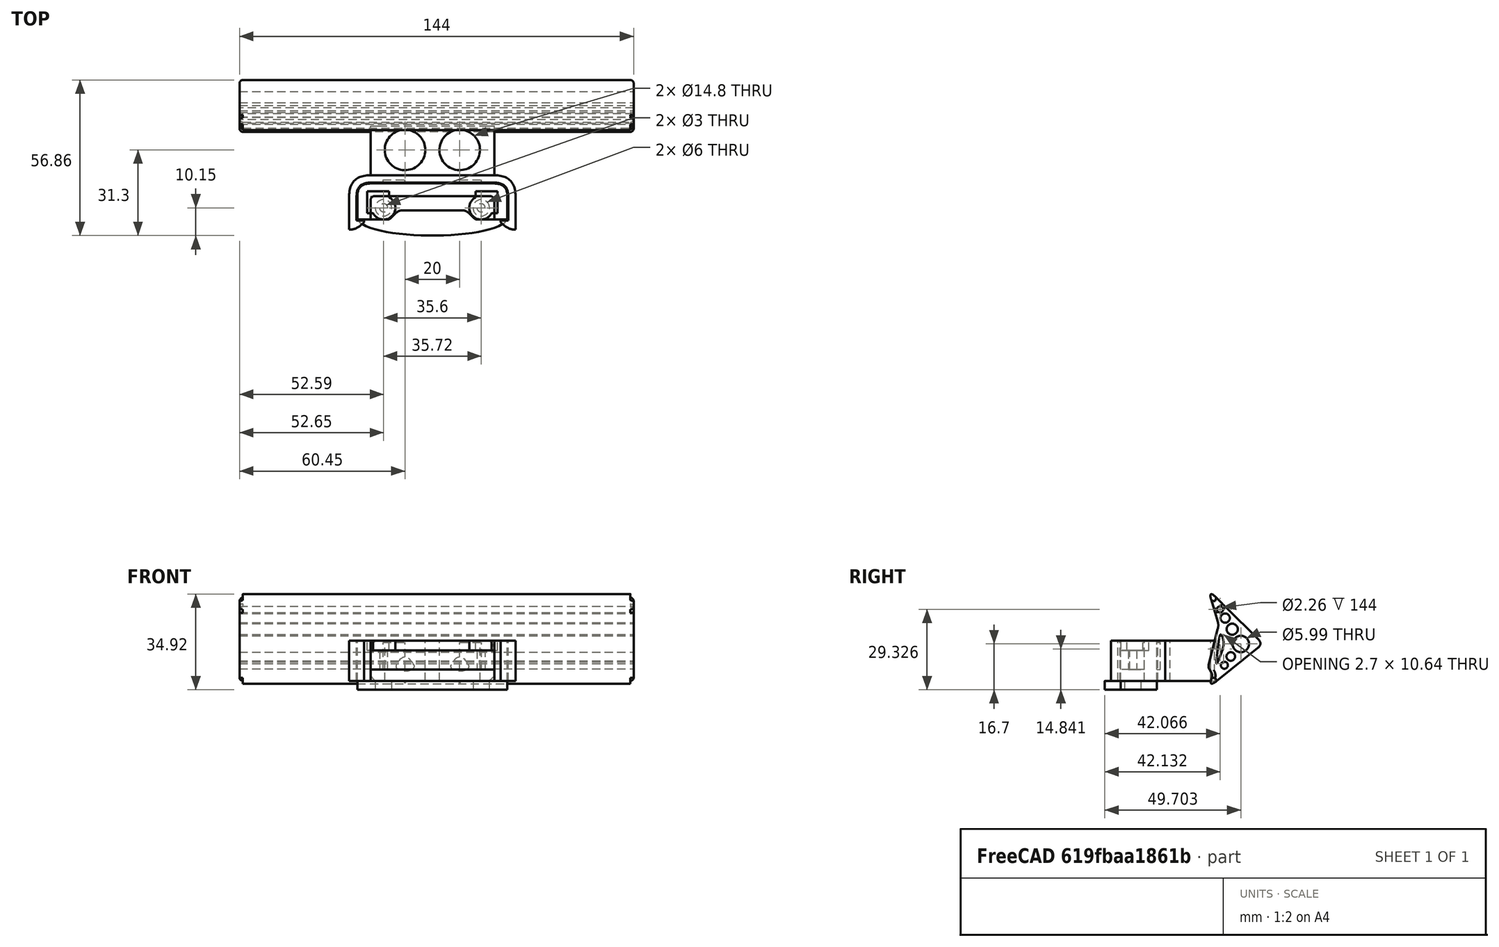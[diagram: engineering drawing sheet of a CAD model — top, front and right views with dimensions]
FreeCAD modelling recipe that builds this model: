
FCSTD DOCUMENT  (FreeCAD 0.19R0.19.2)
Label: 037
License: All rights reserved
LicenseURL: http://en.wikipedia.org/wiki/All_rights_reserved
objects: Sketcher::SketchObject×6, Part::Extrusion×6, Part::Cylinder×4, Part::Box×3, Part::Fillet×3, Part::MultiFuse×2, Part::Cut×2
note: 26 computed .brp shape members not serialized (recipe doc carries the construction recipe); baked Part::Feature solids carry a one-line shape summary decoded from their .brp

FEATURE [Sketcher::SketchObject] Sketch  label="attatchmentPiece"
  FullyConstrained = true
  sketch-geometry (20):
    g0: Circle CenterX=16.25 CenterY=0 CenterZ=0 NormalX=0 NormalY=0 NormalZ=1 AngleXU=0 Radius=1.5
    g1: LineSegment StartX=21.05 StartY=0 StartZ=0 EndX=21.05 EndY=-1 EndZ=0
    g2: LineSegment StartX=21.05 StartY=-1 StartZ=0 EndX=21.05 EndY=-4.3 EndZ=0
    g3: LineSegment StartX=-24.15 StartY=4.3 StartZ=0 EndX=21.05 EndY=4.3 EndZ=0
    g4: LineSegment StartX=21.05 StartY=0 StartZ=0 EndX=21.05 EndY=4.3 EndZ=0
    g5-g8: Circle x4 (B-spline internal-alignment scaffolding for g9; pole/knot coordinates omitted)
    g9: BSplineCurve PolesCount=4 KnotsCount=2 Degree=3 IsPeriodic=0
    g10: GeomPoint X=10.05 Y=-1 Z=0
    g11: GeomPoint X=14.55 Y=-4.3 Z=0
    g12: LineSegment StartX=10.05 StartY=-1 StartZ=0 EndX=-10.05 EndY=-1 EndZ=0
    g13: LineSegment StartX=14.55 StartY=-4.3 StartZ=0 EndX=21.05 EndY=-4.3 EndZ=0
    g14: LineSegment StartX=-24.15 StartY=4.3 StartZ=0 EndX=-24.15 EndY=-4.3 EndZ=0
    g15: LineSegment StartX=-13.15 StartY=-1 StartZ=0 EndX=-10.05 EndY=-1 EndZ=0
    g16: LineSegment StartX=-24.15 StartY=-4.3 StartZ=0 EndX=-19.35 EndY=-4.3 EndZ=0
    g17: Circle CenterX=-19.35 CenterY=0 CenterZ=0 NormalX=0 NormalY=0 NormalZ=1 AngleXU=0 Radius=1.5
    g18: LineSegment StartX=-19.35 StartY=-4.3 StartZ=0 EndX=-17.65 EndY=-4.3 EndZ=0
    g19: BSplineCurve PolesCount=4 KnotsCount=2 Degree=3 IsPeriodic=0
  constraints (41):
    c: Block(g0)
    c: Vertical(g1)
    c: Coincident(g2,g1)
    c: Vertical(g2)
    c: Block(g1)
    c: Horizontal(g3)
    c: Vertical(g4)
    c: Coincident(g4,g3)
    c: Block(g3)
    c: Block(g4)
    c: Weight(g5) = 1
    c: Equal(g5,g6)
    c: Equal(g5,g7)
    c: Equal(g5,g8)
    c: InternalAlignment(g5-g8 -> g9) x4
    c: InternalAlignment(g10,g9)
    c: InternalAlignment(g11,g9)
    c: Block(g9)
    c: Coincident(g12,g9)
    c: Horizontal(g12)
    c: Coincident(g13,g9)
    c: Coincident(g13,g2)
    c: Horizontal(g13)
    c: Distance(g3) = 45.2
    c: Coincident(g14,g3)
    c: Vertical(g14)
    c: Horizontal(g15)
    c: Distance(g15) = 3.1
    c: Block(g17)
    c: Horizontal(g16)
    c: Block(g19)
    c: Coincident(g18,g16)
    c: Coincident(g18,g19)
    c: Horizontal(g18)
    c: Block(g18)
    c: Coincident(g19,g15)
    c: Block(g16)
    c: Block(g12)
    c: Block(g14)
    c: Distance(g16) = 4.8
    c: Distance(g18) = 1.7
FEATURE [Part::Extrusion] Extrude  label="attatchmentPiece001"
  Base = -> Sketch
  Dir = (0,0,1)
  DirMode = 2
  FaceMakerClass = Part::FaceMakerBullseye
  LengthFwd = 7
  LengthRev = 0
  Solid = true
  Symmetric = false
FEATURE [Sketcher::SketchObject] Sketch001  label="attatchmentPieceSurround"
  FullyConstrained = true
  sketch-geometry (18):
    g0: LineSegment StartX=25.85 StartY=-4.3 StartZ=0 EndX=21.05 EndY=-4.3 EndZ=0
    g1: LineSegment StartX=25.85 StartY=-4.3 StartZ=0 EndX=25.85 EndY=4.3 EndZ=0
    g2: LineSegment StartX=-21.05 StartY=8.9 StartZ=0 EndX=21.05 EndY=8.9 EndZ=0
    g3: Circle CenterX=21.05 CenterY=8.9 CenterZ=0 NormalX=0 NormalY=0 NormalZ=1 AngleXU=0 Radius=1
    g4: Circle CenterX=25.85 CenterY=8.9 CenterZ=0 NormalX=0 NormalY=0 NormalZ=1 AngleXU=0 Radius=1
    g5: Circle CenterX=25.85 CenterY=4.3 CenterZ=0 NormalX=0 NormalY=0 NormalZ=1 AngleXU=0 Radius=1
    g6: BSplineCurve PolesCount=3 KnotsCount=2 Degree=2 IsPeriodic=0
    g7: GeomPoint X=21.05 Y=8.9 Z=0
    g8: GeomPoint X=25.85 Y=4.3 Z=0
    g9: ArcOfCircle CenterX=19.45 CenterY=2.7 CenterZ=0 NormalX=0 NormalY=0 NormalZ=1 AngleXU=0 Radius=1.6 StartAngle=0 EndAngle=1.5708
    g10: LineSegment StartX=21.05 StartY=2.7 StartZ=0 EndX=21.05 EndY=-4.3 EndZ=0
    g11: BSplineCurve PolesCount=3 KnotsCount=2 Degree=2 IsPeriodic=0
    g12: LineSegment StartX=-28.95 StartY=-4.3 StartZ=0 EndX=-28.95 EndY=4.3 EndZ=0
    g13: LineSegment StartX=-24.15 StartY=-4.3 StartZ=0 EndX=-28.95 EndY=-4.3 EndZ=0
    g14: LineSegment StartX=-24.15 StartY=2.7 StartZ=0 EndX=-24.15 EndY=-4.3 EndZ=0
    g15: ArcOfCircle CenterX=-22.55 CenterY=2.7 CenterZ=0 NormalX=0 NormalY=0 NormalZ=1 AngleXU=0 Radius=1.6 StartAngle=1.5708 EndAngle=3.14159
    g16: LineSegment StartX=-24.15 StartY=8.9 StartZ=0 EndX=-21.05 EndY=8.9 EndZ=0
    g17: LineSegment StartX=-22.55 StartY=4.3 StartZ=0 EndX=19.45 EndY=4.3 EndZ=0
  constraints (38):
    c: Horizontal(g0)
    c: Vertical(g1)
    c: Coincident(g1,g0)
    c: Horizontal(g2)
    c: Distance(g2) = 42.1
    c: Block(g2)
    c: Coincident(g6,g2)
    c: Weight(g3) = 1
    c: Equal(g3,g4)
    c: Equal(g3,g5)
    c: Coincident(g6,g1)
    c: InternalAlignment(g3,g6)
    c: InternalAlignment(g4,g6)
    c: InternalAlignment(g5,g6)
    c: InternalAlignment(g7,g6)
    c: InternalAlignment(g8,g6)
    c: Block(g0)
    c: Block(g6)
    c: Block(g9)
    c: Coincident(g10,g9)
    c: Coincident(g10,g0)
    c: Vertical(g10)
    c: Horizontal(g13)
    c: Coincident(g12,g13)
    c: Vertical(g12)
    c: Coincident(g11,g12)
    c: Block(g12)
    c: Block(g11)
    c: Block(g15)
    c: Coincident(g14,g15)
    c: Coincident(g14,g13)
    c: Vertical(g14)
    c: Coincident(g16,g11)
    c: Coincident(g16,g2)
    c: Horizontal(g16)
    c: Coincident(g17,g15)
    c: Coincident(g17,g9)
    c: Horizontal(g17)
FEATURE [Part::Extrusion] Extrude001  label="attatchmentPieceSurround001"
  Base = -> Sketch001
  Dir = (0,0,1)
  DirMode = 2
  FaceMakerClass = Part::FaceMakerBullseye
  LengthFwd = 14.7
  LengthRev = 0
  Placement = pos=(0,0,-4.1) rot=(0,0,1;0rad)
  Solid = true
  Symmetric = false
FEATURE [Sketcher::SketchObject] Sketch002  label="attatchmentPieceEndScrewHoleCaps"
  FullyConstrained = true
  sketch-geometry (10):
    g0: ArcOfCircle CenterX=16.25 CenterY=0 CenterZ=0 NormalX=0 NormalY=0 NormalZ=1 AngleXU=0 Radius=4.3 StartAngle=2.05456 EndAngle=5.79942
    g1: LineSegment StartX=14.25 StartY=3.80657 StartZ=0 EndX=14.25 EndY=6 EndZ=0
    g2: LineSegment StartX=20.0566 StartY=-2 StartZ=0 EndX=22.25 EndY=-2 EndZ=0
    g3: LineSegment StartX=22.25 StartY=-2 StartZ=0 EndX=22.25 EndY=6 EndZ=0
    g4: LineSegment StartX=14.25 StartY=6 StartZ=0 EndX=22.25 EndY=6 EndZ=0
    g5: LineSegment StartX=-25.35 StartY=-2 StartZ=0 EndX=-25.35 EndY=6 EndZ=0
    g6: LineSegment StartX=-25.35 StartY=-2 StartZ=0 EndX=-23.1566 EndY=-2 EndZ=0
    g7: LineSegment StartX=-17.35 StartY=6 StartZ=0 EndX=-25.35 EndY=6 EndZ=0
    g8: LineSegment StartX=-17.35 StartY=3.80657 StartZ=0 EndX=-17.35 EndY=6 EndZ=0
    g9: ArcOfCircle CenterX=-19.35 CenterY=0 CenterZ=0 NormalX=0 NormalY=0 NormalZ=1 AngleXU=0 Radius=4.3 StartAngle=3.62536 EndAngle=7.37022
  constraints (25):
    c: Block(g0)
    c: Vertical(g1)
    c: Horizontal(g2)
    c: Coincident(g3,g2)
    c: Vertical(g3)
    c: Coincident(g4,g1)
    c: Horizontal(g4)
    c: Coincident(g3,g4)
    c: Block(g4)
    c: Block(g3)
    c: Coincident(g0,g1)
    c: Coincident(g0,g2)
    c: Block(g1)
    c: Block(g9)
    c: Horizontal(g6)
    c: Vertical(g8)
    c: Coincident(g7,g8)
    c: Horizontal(g7)
    c: Coincident(g5,g6)
    c: Vertical(g5)
    c: Coincident(g5,g7)
    c: Block(g7)
    c: Block(g5)
    c: Coincident(g9,g6)
    c: Coincident(g9,g8)
FEATURE [Part::Extrusion] Extrude002  label="attatchmentPieceEndScrewHoleCaps001"
  Base = -> Sketch002
  Dir = (0,0,1)
  DirMode = 2
  FaceMakerClass = Part::FaceMakerBullseye
  LengthFwd = 3.6
  LengthRev = 0
  Placement = pos=(0,0,7) rot=(0,0,1;0rad)
  Solid = true
  Symmetric = false
FEATURE [Sketcher::SketchObject] Sketch003  label="mainBumpperPieceAttatchment"
  FullyConstrained = true
  sketch-geometry (42):
    g0: Circle CenterX=28.85 CenterY=4.3 CenterZ=0 NormalX=0 NormalY=0 NormalZ=1 AngleXU=0 Radius=1
    g1: Circle CenterX=28.85 CenterY=11.9 CenterZ=0 NormalX=0 NormalY=0 NormalZ=1 AngleXU=0 Radius=1
    g2: Circle CenterX=21.05 CenterY=11.9 CenterZ=0 NormalX=0 NormalY=0 NormalZ=1 AngleXU=0 Radius=1
    g3: BSplineCurve PolesCount=3 KnotsCount=2 Degree=2 IsPeriodic=0
    g4: GeomPoint X=28.85 Y=4.3 Z=0
    g5: GeomPoint X=21.05 Y=11.9 Z=0
    g6: LineSegment StartX=-21.05 StartY=11.9 StartZ=0 EndX=21.05 EndY=11.9 EndZ=0
    g7: LineSegment StartX=28.85 StartY=4.3 StartZ=0 EndX=28.85 EndY=-4.3 EndZ=0
    g8: Circle CenterX=21.05 CenterY=9.2 CenterZ=0 NormalX=0 NormalY=0 NormalZ=1 AngleXU=0 Radius=1
    g9: Circle CenterX=26.15 CenterY=9.2 CenterZ=0 NormalX=0 NormalY=0 NormalZ=1 AngleXU=0 Radius=1
    g10: Circle CenterX=26.15 CenterY=4.3 CenterZ=0 NormalX=0 NormalY=0 NormalZ=1 AngleXU=0 Radius=1
    g11: BSplineCurve PolesCount=3 KnotsCount=2 Degree=2 IsPeriodic=0
    g12: GeomPoint X=21.05 Y=9.2 Z=0
    g13: GeomPoint X=26.15 Y=4.3 Z=0
    g14: LineSegment StartX=-21.05 StartY=9.2 StartZ=0 EndX=21.05 EndY=9.2 EndZ=0
    g15: LineSegment StartX=26.15 StartY=-4.3 StartZ=0 EndX=26.15 EndY=4.3 EndZ=0
    g16: LineSegment StartX=26.15 StartY=-4.3 StartZ=0 EndX=26.15 EndY=-4.6 EndZ=0
    g17: LineSegment StartX=23.45 StartY=-4.6 StartZ=0 EndX=26.15 EndY=-4.6 EndZ=0
    g18: LineSegment StartX=28.85 StartY=-4.3 StartZ=0 EndX=28.85 EndY=-7.9 EndZ=0
    g19: LineSegment StartX=23.45 StartY=-4.6 StartZ=0 EndX=23.45 EndY=-5.3 EndZ=0
    g20: Circle CenterX=28.85 CenterY=-7.9 CenterZ=0 NormalX=0 NormalY=0 NormalZ=1 AngleXU=0 Radius=1
    g21: Circle CenterX=26.15 CenterY=-8.2 CenterZ=0 NormalX=0 NormalY=0 NormalZ=1 AngleXU=0 Radius=1
    g22: Circle CenterX=23.45 CenterY=-5.3 CenterZ=0 NormalX=0 NormalY=0 NormalZ=1 AngleXU=0 Radius=1
    g23: BSplineCurve PolesCount=3 KnotsCount=2 Degree=2 IsPeriodic=0
    g24: GeomPoint X=28.85 Y=-7.9 Z=0
    g25: GeomPoint X=23.45 Y=-5.3 Z=0
    g26: LineSegment StartX=-21.05 StartY=9.2 StartZ=0 EndX=-24.15 EndY=9.2 EndZ=0
    g27: BSplineCurve PolesCount=3 KnotsCount=2 Degree=2 IsPeriodic=0
    g28: LineSegment StartX=-29.25 StartY=-4.3 StartZ=0 EndX=-29.25 EndY=-4.6 EndZ=0
    g29: LineSegment StartX=-29.25 StartY=-4.6 StartZ=0 EndX=-26.55 EndY=-4.6 EndZ=0
    g30: LineSegment StartX=-31.95 StartY=-4.3 StartZ=0 EndX=-31.95 EndY=-7.9 EndZ=0
    g31: LineSegment StartX=-26.55 StartY=-4.6 StartZ=0 EndX=-26.55 EndY=-5.3 EndZ=0
    g32: Circle CenterX=-31.95 CenterY=-7.9 CenterZ=0 NormalX=0 NormalY=0 NormalZ=1 AngleXU=0 Radius=1
    g33: Circle CenterX=-29.25 CenterY=-8.2 CenterZ=0 NormalX=0 NormalY=0 NormalZ=1 AngleXU=0 Radius=1
    g34: Circle CenterX=-26.55 CenterY=-5.3 CenterZ=0 NormalX=0 NormalY=0 NormalZ=1 AngleXU=0 Radius=1
    g35: BSplineCurve PolesCount=3 KnotsCount=2 Degree=2 IsPeriodic=0
    g36: GeomPoint X=-31.95 Y=-7.9 Z=0
    g37: GeomPoint X=-26.55 Y=-5.3 Z=0
    g38: LineSegment StartX=-31.95 StartY=4.3 StartZ=0 EndX=-31.95 EndY=-4.3 EndZ=0
    g39: LineSegment StartX=-29.25 StartY=-4.3 StartZ=0 EndX=-29.25 EndY=4.3 EndZ=0
    g40: BSplineCurve PolesCount=3 KnotsCount=2 Degree=2 IsPeriodic=0
    g41: LineSegment StartX=-21.05 StartY=11.9 StartZ=0 EndX=-24.15 EndY=11.9 EndZ=0
  constraints (78):
    c: Weight(g0) = 1
    c: Equal(g0,g1)
    c: Equal(g0,g2)
    c: InternalAlignment(g0,g3)
    c: InternalAlignment(g1,g3)
    c: InternalAlignment(g2,g3)
    c: InternalAlignment(g4,g3)
    c: InternalAlignment(g5,g3)
    c: Block(g3)
    c: Horizontal(g6)
    c: Vertical(g7)
    c: Block(g7)
    c: Block(g6)
    c: Weight(g8) = 1
    c: Equal(g8,g9)
    c: Equal(g8,g10)
    c: InternalAlignment(g8,g11)
    c: InternalAlignment(g9,g11)
    c: InternalAlignment(g10,g11)
    c: InternalAlignment(g12,g11)
    c: InternalAlignment(g13,g11)
    c: Horizontal(g14)
    c: Vertical(g15)
    c: Block(g11)
    c: Block(g15)
    c: Block(g14)
    c: Coincident(g16,g15)
    c: Vertical(g16)
    c: Distance(g16) = 0.3
    c: Horizontal(g17)
    c: Coincident(g17,g16)
    c: Coincident(g18,g7)
    c: Vertical(g18)
    c: Distance(g18) = 3.6
    c: Vertical(g19)
    c: Coincident(g19,g17)
    c: Coincident(g23,g18)
    c: Weight(g20) = 1
    c: Equal(g20,g21)
    c: Equal(g20,g22)
    c: Coincident(g23,g19)
    c: InternalAlignment(g20,g23)
    c: InternalAlignment(g21,g23)
    c: InternalAlignment(g22,g23)
    c: InternalAlignment(g24,g23)
    c: InternalAlignment(g25,g23)
    c: Block(g23)
    c: Horizontal(g26)
    c: Distance(g26) = 3.1
    c: Block(g27)
    c: Vertical(g38)
    c: Block(g38)
    c: Vertical(g39)
    c: Block(g40)
    c: Block(g39)
    c: Vertical(g28)
    c: Coincident(g28,g39)
    c: Coincident(g29,g28)
    c: Horizontal(g29)
    c: Vertical(g30)
    c: Coincident(g30,g38)
    c: Coincident(g31,g29)
    c: Vertical(g31)
    c: Coincident(g35,g30)
    c: Equal(g32,g33)
    c: Equal(g32,g34)
    c: Coincident(g35,g31)
    c: InternalAlignment(g32,g35)
    c: InternalAlignment(g33,g35)
    c: InternalAlignment(g34,g35)
    c: InternalAlignment(g36,g35)
    c: InternalAlignment(g37,g35)
    c: Block(g35)
    c: Coincident(g40,g26)
    c: Block(g29)
    c: Horizontal(g41)
    c: Equal(g26,g41) = 3.1
    c: Coincident(g41,g6)
FEATURE [Part::Box] Box  label="bumpperExtension"
  AttacherType = Attacher::AttachEngine3D
  Height = 14.7
  Length = 45.2
  Placement = pos=(-24.15,11.9,-4.1) rot=(0,0,1;0rad)
  Width = 18
FEATURE [Sketcher::SketchObject] Sketch004  label="bumpperMain"
  FullyConstrained = true
  Placement = pos=(0,0,0) rot=(0.57735,0.57735,0.57735;2.0944rad)
  sketch-geometry (62):
    g0: Circle CenterX=-3.12329 CenterY=2.49901 CenterZ=0 NormalX=0 NormalY=0 NormalZ=1 AngleXU=0 Radius=1
    g1: Circle CenterX=0 CenterY=0 CenterZ=0 NormalX=0 NormalY=0 NormalZ=1 AngleXU=0 Radius=1
    g2: Circle CenterX=-1.35243 CenterY=3.60648 CenterZ=0 NormalX=0 NormalY=0 NormalZ=1 AngleXU=0 Radius=1
    g3: BSplineCurve PolesCount=3 KnotsCount=2 Degree=2 IsPeriodic=0
    g4: GeomPoint X=-3.12329 Y=2.49901 Z=0
    g5: GeomPoint X=-1.35243 Y=3.60648 Z=0
    g6: Circle CenterX=-2.83953 CenterY=33.0261 CenterZ=0 NormalX=0 NormalY=0 NormalZ=1 AngleXU=0 Radius=1
    g7: Circle CenterX=0 CenterY=35.8434 CenterZ=0 NormalX=0 NormalY=0 NormalZ=1 AngleXU=0 Radius=1
    g8: Circle CenterX=-1.15771 CenterY=32.0146 CenterZ=0 NormalX=0 NormalY=0 NormalZ=1 AngleXU=0 Radius=1
    g9: BSplineCurve PolesCount=3 KnotsCount=2 Degree=2 IsPeriodic=0
    g10: GeomPoint X=-2.83953 Y=33.0261 Z=0
    g11: GeomPoint X=-1.15771 Y=32.0146 Z=0
    g12: Circle CenterX=-18.2963 CenterY=17.6904 CenterZ=0 NormalX=0 NormalY=0 NormalZ=1 AngleXU=0 Radius=1
    g13: Circle CenterX=-20 CenterY=16 CenterZ=0 NormalX=0 NormalY=0 NormalZ=1 AngleXU=0 Radius=1
    g14: Circle CenterX=-18.1259 CenterY=14.5008 CenterZ=0 NormalX=0 NormalY=0 NormalZ=1 AngleXU=0 Radius=1
    g15: BSplineCurve PolesCount=3 KnotsCount=2 Degree=2 IsPeriodic=0
    g16: GeomPoint X=-18.2963 Y=17.6904 Z=0
    g17: GeomPoint X=-18.1259 Y=14.5008 Z=0
    g18: LineSegment StartX=-18.2963 StartY=17.6904 StartZ=0 EndX=-2.83953 EndY=33.0261 EndZ=0
    g19: LineSegment StartX=-18.1259 StartY=14.5008 StartZ=0 EndX=-3.12329 EndY=2.49901 EndZ=0
    g20: Circle CenterX=-11.9527 CenterY=16 CenterZ=0 NormalX=0 NormalY=0 NormalZ=1 AngleXU=0 Radius=2.99582
    g21: Circle CenterX=-8.803 CenterY=21.3731 CenterZ=0 NormalX=0 NormalY=0 NormalZ=1 AngleXU=0 Radius=2.03939
    g22: Circle CenterX=-6.23123 CenterY=25.4475 CenterZ=0 NormalX=0 NormalY=0 NormalZ=1 AngleXU=0 Radius=1.69309
    g23: Circle CenterX=-4.38186 CenterY=28.6261 CenterZ=0 NormalX=0 NormalY=0 NormalZ=1 AngleXU=0 Radius=1.13029
    g24: Circle CenterX=-8.28033 CenterY=11.4296 CenterZ=0 NormalX=0 NormalY=0 NormalZ=1 AngleXU=0 Radius=1.57213
    g25: Circle CenterX=-5.93972 CenterY=8.22213 CenterZ=0 NormalX=0 NormalY=0 NormalZ=1 AngleXU=0 Radius=1.28743
    g26: Circle CenterX=-3.47023 CenterY=24.3665 CenterZ=0 NormalX=0 NormalY=0 NormalZ=1 AngleXU=0 Radius=1
    g27: Circle CenterX=-3.90437 CenterY=22.9307 CenterZ=0 NormalX=0 NormalY=0 NormalZ=1 AngleXU=0 Radius=1
    g28: Circle CenterX=-3.53772 CenterY=21.4762 CenterZ=0 NormalX=0 NormalY=0 NormalZ=1 AngleXU=0 Radius=1
    g29: BSplineCurve PolesCount=3 KnotsCount=2 Degree=2 IsPeriodic=0
    g30: GeomPoint X=-3.47023 Y=24.3665 Z=0
    g31: GeomPoint X=-3.53772 Y=21.4762 Z=0
    g32: LineSegment StartX=-1.15771 StartY=32.0146 StartZ=0 EndX=-3.47023 EndY=24.3665 EndZ=0
    g33: Circle CenterX=-5.41867 CenterY=17.9226 CenterZ=0 NormalX=0 NormalY=0 NormalZ=1 AngleXU=0 Radius=1
    g34: Circle CenterX=-6 CenterY=16 CenterZ=0 NormalX=0 NormalY=0 NormalZ=1 AngleXU=0 Radius=1
    g35: Circle CenterX=-5.22753 CenterY=13.9401 CenterZ=0 NormalX=0 NormalY=0 NormalZ=1 AngleXU=0 Radius=1
    g36: BSplineCurve PolesCount=3 KnotsCount=2 Degree=2 IsPeriodic=0
    g37: GeomPoint X=-5.41867 Y=17.9226 Z=0
    g38: GeomPoint X=-5.22753 Y=13.9401 Z=0
    g39: Circle CenterX=-3.98946 CenterY=10.6386 CenterZ=0 NormalX=0 NormalY=0 NormalZ=1 AngleXU=0 Radius=1
    g40: Circle CenterX=-2.58497 CenterY=6.89324 CenterZ=0 NormalX=0 NormalY=0 NormalZ=1 AngleXU=0 Radius=1
    g41: Circle CenterX=-3.11001 CenterY=10.8586 CenterZ=0 NormalX=0 NormalY=0 NormalZ=1 AngleXU=0 Radius=1
    g42: BSplineCurve PolesCount=3 KnotsCount=2 Degree=2 IsPeriodic=0
    g43: GeomPoint X=-3.98946 Y=10.6386 Z=0
    g44: GeomPoint X=-3.11001 Y=10.8586 Z=0
    g45: Circle CenterX=-1.35243 CenterY=3.60648 CenterZ=0 NormalX=0 NormalY=0 NormalZ=1 AngleXU=0 Radius=1
    g46: Circle CenterX=-1.76142 CenterY=4.69712 CenterZ=0 NormalX=0 NormalY=0 NormalZ=1 AngleXU=0 Radius=1
    g47: Circle CenterX=-1.05937 CenterY=5.79125 CenterZ=0 NormalX=0 NormalY=0 NormalZ=1 AngleXU=0 Radius=1
    g48: BSplineCurve PolesCount=3 KnotsCount=2 Degree=2 IsPeriodic=0
    g49: GeomPoint X=-1.35243 Y=3.60648 Z=0
    g50: GeomPoint X=-1.05937 Y=5.79125 Z=0
    g51: Circle CenterX=-0.519336 CenterY=6.6329 CenterZ=0 NormalX=0 NormalY=0 NormalZ=1 AngleXU=0 Radius=1
    g52: Circle CenterX=0 CenterY=7.44228 CenterZ=0 NormalX=0 NormalY=0 NormalZ=1 AngleXU=0 Radius=1
    g53: Circle CenterX=-0.244436 CenterY=8.41194 CenterZ=0 NormalX=0 NormalY=0 NormalZ=1 AngleXU=0 Radius=1
    g54: BSplineCurve PolesCount=3 KnotsCount=2 Degree=2 IsPeriodic=0
    g55: GeomPoint X=-0.519336 Y=6.6329 Z=0
    g56: GeomPoint X=-0.244436 Y=8.41194 Z=0
    g57: LineSegment StartX=-3.53772 StartY=21.4762 StartZ=0 EndX=-0.244436 EndY=8.41194 EndZ=0
    g58: LineSegment StartX=-5.22753 StartY=13.9401 StartZ=0 EndX=-3.98946 EndY=10.6386 EndZ=0
    g59: LineSegment StartX=-1.05937 StartY=5.79125 StartZ=0 EndX=-0.519336 EndY=6.6329 EndZ=0
    g60: BSplineCurve PolesCount=3 KnotsCount=2 Degree=2 IsPeriodic=0
    g61: LineSegment StartX=-4.0304 StartY=17.8099 StartZ=0 EndX=-3.11001 EndY=10.8586 EndZ=0
  constraints (96):
    c: Weight(g0) = 1
    c: Equal(g0,g1)
    c: Equal(g0,g2)
    c: InternalAlignment(g0,g3)
    c: InternalAlignment(g1,g3)
    c: InternalAlignment(g2,g3)
    c: InternalAlignment(g4,g3)
    c: InternalAlignment(g5,g3)
    c: Block(g3)
    c: Weight(g6) = 1
    c: Equal(g6,g7)
    c: Equal(g6,g8)
    c: InternalAlignment(g6,g9)
    c: InternalAlignment(g7,g9)
    c: InternalAlignment(g8,g9)
    c: InternalAlignment(g10,g9)
    c: InternalAlignment(g11,g9)
    c: Block(g9)
    c: Weight(g12) = 1
    c: Equal(g12,g13)
    c: Equal(g12,g14)
    c: InternalAlignment(g12,g15)
    c: InternalAlignment(g13,g15)
    c: InternalAlignment(g14,g15)
    c: InternalAlignment(g16,g15)
    c: InternalAlignment(g17,g15)
    c: Block(g15)
    c: Coincident(g18,g15)
    c: Coincident(g18,g9)
    c: Coincident(g19,g15)
    c: Coincident(g19,g3)
    c: Block(g25)
    c: Block(g24)
    c: Block(g20)
    c: Block(g21)
    c: Block(g22)
    c: Block(g23)
    c: Weight(g26) = 1
    c: Equal(g26,g27)
    c: Equal(g26,g28)
    c: InternalAlignment(g26,g29)
    c: InternalAlignment(g27,g29)
    c: InternalAlignment(g28,g29)
    c: InternalAlignment(g30,g29)
    c: InternalAlignment(g31,g29)
    c: Block(g29)
    c: Coincident(g32,g9)
    c: Coincident(g32,g29)
    c: Weight(g33) = 1
    c: Equal(g33,g34)
    c: Equal(g33,g35)
    c: InternalAlignment(g33,g36)
    c: InternalAlignment(g34,g36)
    c: InternalAlignment(g35,g36)
    c: InternalAlignment(g37,g36)
    c: InternalAlignment(g38,g36)
    c: Block(g36)
    c: Weight(g39) = 1
    c: Equal(g39,g40)
    c: Equal(g39,g41)
    c: InternalAlignment(g39,g42)
    c: InternalAlignment(g40,g42)
    c: InternalAlignment(g41,g42)
    c: InternalAlignment(g43,g42)
    c: InternalAlignment(g44,g42)
    c: Block(g42)
    c: Coincident(g48,g3)
    c: Weight(g45) = 1
    c: Equal(g45,g46)
    c: Equal(g45,g47)
    c: InternalAlignment(g45,g48)
    c: InternalAlignment(g46,g48)
    c: InternalAlignment(g47,g48)
    c: InternalAlignment(g49,g48)
    c: InternalAlignment(g50,g48)
    c: Block(g48)
    c: Weight(g51) = 1
    c: Equal(g51,g52)
    c: Equal(g51,g53)
    c: InternalAlignment(g51,g54)
    c: InternalAlignment(g52,g54)
    c: InternalAlignment(g53,g54)
    c: InternalAlignment(g55,g54)
    c: InternalAlignment(g56,g54)
    c: Block(g54)
    c: Coincident(g57,g29)
    c: Coincident(g57,g54)
    c: Block(g57)
    c: Coincident(g58,g36)
    c: Coincident(g58,g42)
    c: Coincident(g59,g48)
    c: Coincident(g59,g54)
    c: Block(g60)
    c: Coincident(g60,g36)
    c: Coincident(g61,g60)
    c: Coincident(g61,g42)
FEATURE [Part::Extrusion] Extrude004  label="bumpperMain001"
  Base = -> Sketch004
  Dir = (1,0,0)
  DirMode = 2
  FaceMakerClass = Part::FaceMakerBullseye
  LengthFwd = 144
  LengthRev = 0
  Placement = pos=(72,27.6,-6.6) rot=(0,0,1;3.14159rad)
  Solid = true
  Symmetric = false
FEATURE [Sketcher::SketchObject] Sketch005  label="attatchmentPieceBottom"
  FullyConstrained = true
  sketch-geometry (20):
    g0: LineSegment StartX=25.85 StartY=-4.3 StartZ=0 EndX=25.85 EndY=4.3 EndZ=0
    g1: LineSegment StartX=-21.05 StartY=8.9 StartZ=0 EndX=21.05 EndY=8.9 EndZ=0
    g2: Circle CenterX=21.05 CenterY=8.9 CenterZ=0 NormalX=0 NormalY=0 NormalZ=1 AngleXU=0 Radius=1
    g3: Circle CenterX=25.85 CenterY=8.9 CenterZ=0 NormalX=0 NormalY=0 NormalZ=1 AngleXU=0 Radius=1
    g4: Circle CenterX=25.85 CenterY=4.3 CenterZ=0 NormalX=0 NormalY=0 NormalZ=1 AngleXU=0 Radius=1
    g5: BSplineCurve PolesCount=3 KnotsCount=2 Degree=2 IsPeriodic=0
    g6: GeomPoint X=21.05 Y=8.9 Z=0
    g7: GeomPoint X=25.85 Y=4.3 Z=0
    g8: BSplineCurve PolesCount=3 KnotsCount=2 Degree=2 IsPeriodic=0
    g9: LineSegment StartX=-28.95 StartY=-4.3 StartZ=0 EndX=-28.95 EndY=4.3 EndZ=0
    g10: LineSegment StartX=-24.15 StartY=8.9 StartZ=0 EndX=-21.05 EndY=8.9 EndZ=0
    g11: Circle CenterX=-19.41 CenterY=0 CenterZ=0 NormalX=0 NormalY=0 NormalZ=1 AngleXU=0 Radius=3
    g12: Circle CenterX=16.3103 CenterY=0 CenterZ=0 NormalX=0 NormalY=0 NormalZ=1 AngleXU=0 Radius=3
    g13-g16: Circle x4 (B-spline internal-alignment scaffolding for g17; pole/knot coordinates omitted)
    g17: BSplineCurve PolesCount=4 KnotsCount=2 Degree=3 IsPeriodic=0
    g18: GeomPoint X=-28.95 Y=-4.3 Z=0
    g19: GeomPoint X=25.85 Y=-4.3 Z=0
  constraints (36):
    c: Vertical(g0)
    c: Horizontal(g1)
    c: Distance(g1) = 42.1
    c: Block(g1)
    c: Coincident(g5,g1)
    c: Weight(g2) = 1
    c: Equal(g2,g3)
    c: Equal(g2,g4)
    c: Coincident(g5,g0)
    c: InternalAlignment(g2,g5)
    c: InternalAlignment(g3,g5)
    c: InternalAlignment(g4,g5)
    c: InternalAlignment(g6,g5)
    c: InternalAlignment(g7,g5)
    c: Block(g5)
    c: Vertical(g9)
    c: Coincident(g8,g9)
    c: Block(g9)
    c: Block(g8)
    c: Coincident(g10,g8)
    c: Coincident(g10,g1)
    c: Horizontal(g10)
    c: PointOnObject(g12,g-1)
    c: PointOnObject(g11,g-1)
    c: Block(g11)
    c: Block(g12)
    c: Coincident(g17,g9)
    c: Weight(g13) = 1
    c: Equal(g13,g14)
    c: Equal(g13,g15)
    c: Equal(g13,g16)
    c: Coincident(g17,g0)
    c: InternalAlignment(g13-g16 -> g17) x4
    c: InternalAlignment(g18,g17)
    c: InternalAlignment(g19,g17)
    c: Block(g17)
FEATURE [Part::Extrusion] Extrude005  label="attatchmentPieceBottom001"
  Base = -> Sketch005
  Dir = (0,0,1)
  DirMode = 2
  FaceMakerClass = Part::FaceMakerBullseye
  LengthFwd = 3.2
  LengthRev = 0
  Placement = pos=(0,0,-7.3) rot=(0,0,1;0rad)
  Solid = true
  Symmetric = false
FEATURE [Part::Extrusion] Extrude006  label="mainBumpperPieceAttatchment001"
  Base = -> Sketch003
  Dir = (0,0,1)
  DirMode = 2
  FaceMakerClass = Part::FaceMakerBullseye
  LengthFwd = 14.7
  LengthRev = 0
  Placement = pos=(0,0,-4.1) rot=(0,0,1;0rad)
  Solid = true
  Symmetric = false
FEATURE [Part::Cylinder] Cylinder  label="removeFromBumpperExtension"
  Angle = 360
  AttacherType = Attacher::AttachEngine3D
  Height = 20
  Placement = pos=(8.45,21.15,-8) rot=(0,0,1;0rad)
  Radius = 7.4
FEATURE [Part::Cylinder] Cylinder001  label="removeFromBumpperExtension001"
  Angle = 360
  AttacherType = Attacher::AttachEngine3D
  Height = 20
  Placement = pos=(-11.55,21.15,-8) rot=(0,0,1;0rad)
  Radius = 7.4
FEATURE [Part::MultiFuse] Fusion  label="removeFromBumpperExtension002"
  Shapes = -> [Cylinder,Cylinder001]
FEATURE [Part::Cylinder] Cylinder002  label="removeFromBumpperExtension004"
  Angle = 360
  AttacherType = Attacher::AttachEngine3D
  Height = 20
  Placement = pos=(8.45,21.15,-8) rot=(0,0,1;0rad)
  Radius = 7.4
FEATURE [Part::Cylinder] Cylinder003  label="removeFromBumpperExtension005"
  Angle = 360
  AttacherType = Attacher::AttachEngine3D
  Height = 20
  Placement = pos=(-11.55,21.15,-8) rot=(0,0,1;0rad)
  Radius = 7.4
FEATURE [Part::MultiFuse] Fusion001  label="removeFromBumpperMain"
  Shapes = -> [Cylinder002,Cylinder003]
FEATURE [Part::Cut] Cut  label="bumpperExtension001"
  Base = -> Box
  Tool = -> Fusion
FEATURE [Part::Cut] Cut001  label="bumpperMain002"
  Base = -> Extrude004
  Tool = -> Fusion001
FEATURE [Part::Fillet] Fillet  label="bumpperExtension002"
  Base = -> Cut
  Edges = 4 edges r=3: [Edge2,Edge4,Edge9,Edge14]
FEATURE [Part::Fillet] Fillet001
  Base = -> Cut001
  Edges = 11 edges r=1.2: [Edge4,Edge7,Edge10,Edge30,Edge31,Edge32,Edge33,Edge34,Edge35,Edge36,Edge37]
FEATURE [Part::Fillet] Fillet002  label="bumpperMain003"
  Base = -> Fillet001
  Edges = 11 edges r=1.2: [Edge4,Edge9,Edge13,Edge14,Edge15,Edge16,Edge17,Edge18,Edge19,Edge20,Edge21]
FEATURE [Part::Box] Box001  label="Cube"
  AttacherType = Attacher::AttachEngine3D
  Height = 10
  Length = 8
  Placement = pos=(8.45,8.9,0) rot=(0,0,1;0rad)
  Width = 1.3
FEATURE [Part::Box] Box002  label="Cube001"
  AttacherType = Attacher::AttachEngine3D
  Height = 10
  Length = 8
  Placement = pos=(-19.55,8.9,0) rot=(0,0,1;0rad)
  Width = 1.3
